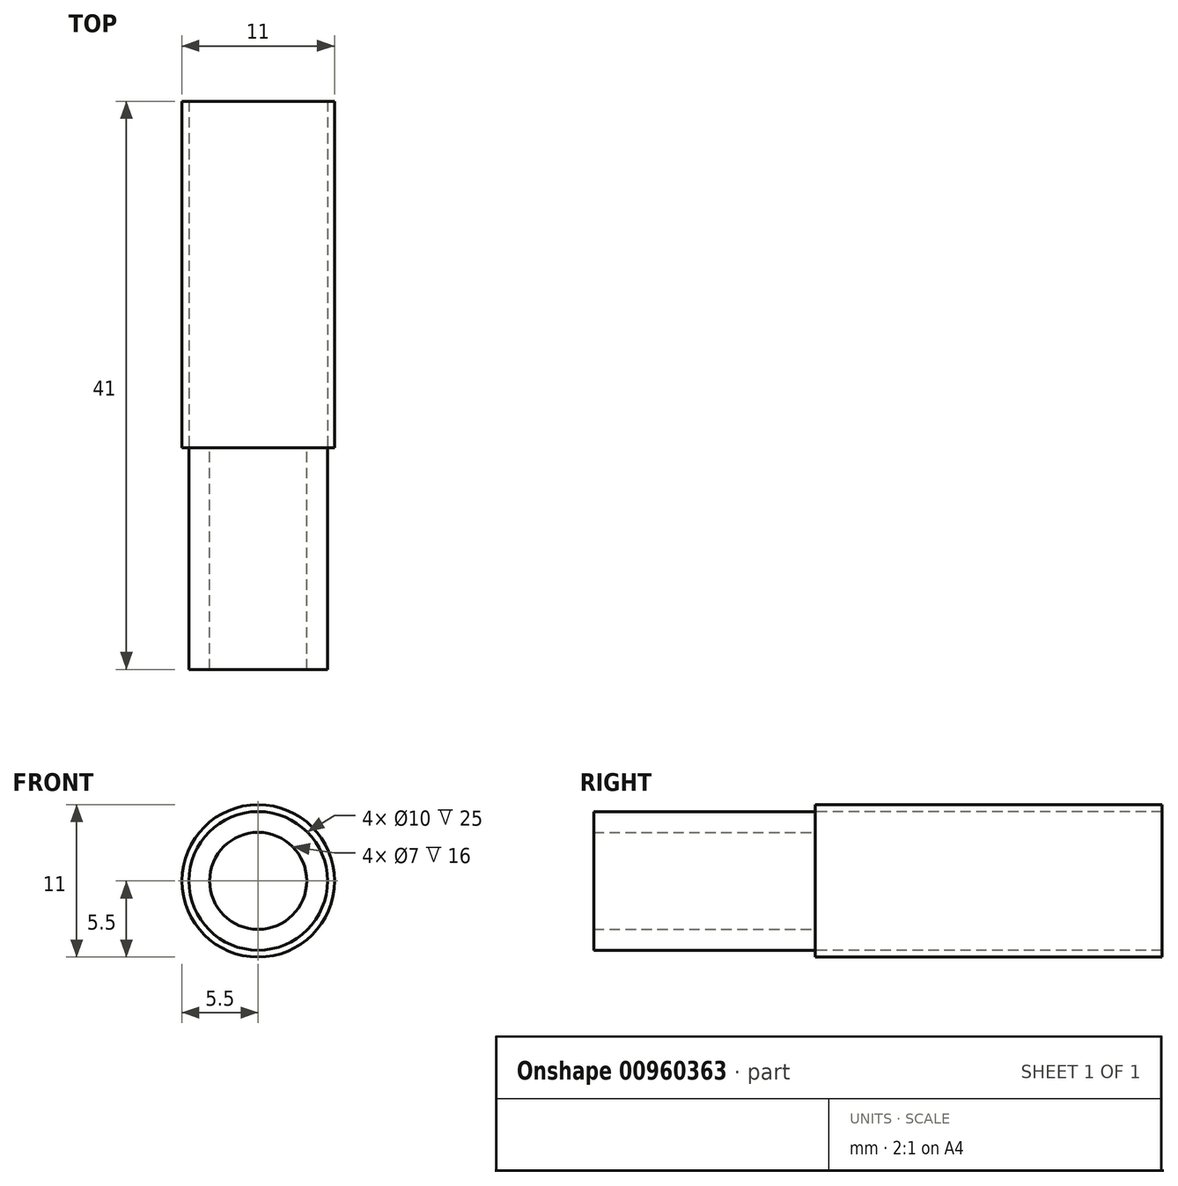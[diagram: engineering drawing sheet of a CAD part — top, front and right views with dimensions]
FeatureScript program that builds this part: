
annotation { "Feature Type Name" : "Feature", "Feature Type Description" : "" }
export const myFeature = defineFeature(function(context is Context, id is Id, definition is map)
    precondition{}
    {
        {
            var Q0;
            Q0=qCreatedBy(makeId("Front.planeOp"),FACE);
            var Q1;
            Q1=qCreatedBy(makeId("Front.planeOp"),FACE);
            var Q2;
            Q2=qCreatedBy(makeId("Front.planeOp"),FACE);
            var sketch = newSketch(context, id + "F0", { "sketchPlane" : qUnion([Q0, Q1, Q2])});
            skCircle(sketch, "E0", {"center": v(0, 0) * mm, "radius": 3.5 * mm});
            skCircle(sketch, "E1", {"center": v(0, 0) * mm, "radius": 5 * mm});
            skCircle(sketch, "E2", {"center": v(0, 0) * mm, "radius": 6.5 * mm});
            skCircle(sketch, "E3", {"center": v(0, 0) * mm, "radius": 5.5 * mm});
            skSolve(sketch);
        }
        {
            var Q0;
            Q0=makeQuery(id+"F0.imprint","IMPRINT",FACE,{"disambiguationData":[TD([[makeQuery(id+"F0.imprint","IMPRINT",EDGE,{"derivedFrom":sQuery(id+"F0.wireOp",EDGE,"E0")}),-1.0]])]});
            extrude(context, id + "F1", {"entities" : qUnion([Q0]), "depth" : 16 * mm, "offsetDistance" : 25.4 * mm});
        }
        {
            var Q0;
            Q0=makeQuery(id+"F0.imprint","IMPRINT",FACE,{"disambiguationData":[TD([[makeQuery(id+"F0.imprint","IMPRINT",EDGE,{"derivedFrom":sQuery(id+"F0.wireOp",EDGE,"E1")}),-1.0]])]});
            extrude(context, id + "F2", {"entities" : qUnion([Q0]), "depth" : -25 * mm, "offsetDistance" : 25.4 * mm});
        }
    });
